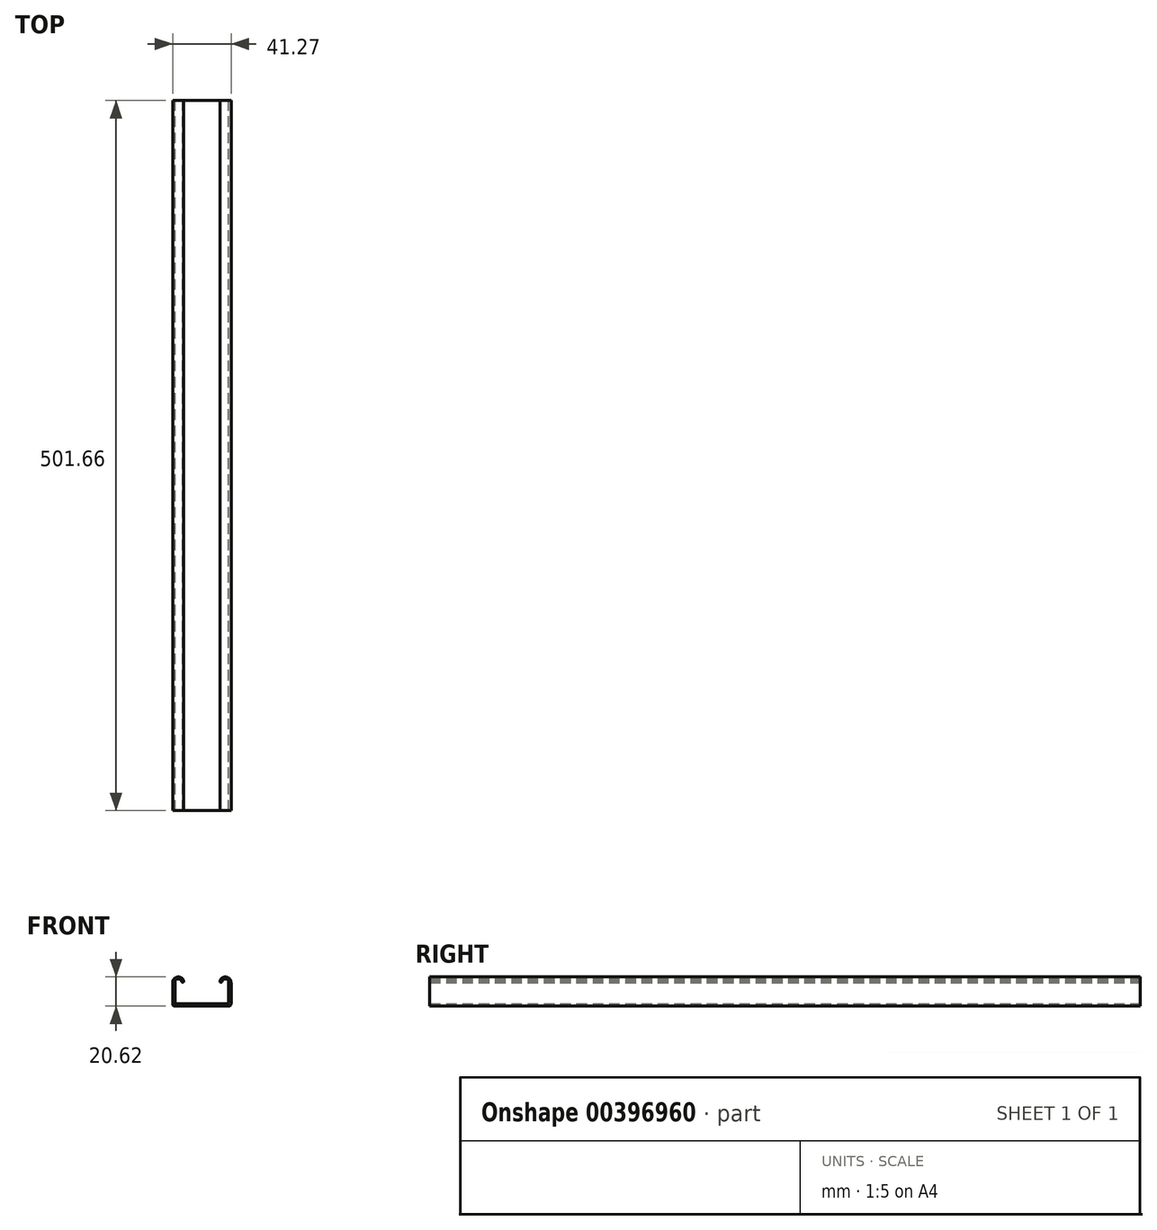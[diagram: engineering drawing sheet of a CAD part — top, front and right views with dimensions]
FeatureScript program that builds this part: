
annotation { "Feature Type Name" : "Feature", "Feature Type Description" : "" }
export const myFeature = defineFeature(function(context is Context, id is Id, definition is map)
    precondition{}
    {
        {
            var Q0;
            Q0=qCreatedBy(makeId("Front.planeOp"),FACE);
            var sketch = newSketch(context, id + "F0", { "sketchPlane" : qUnion([Q0])});
            skLineSegment(sketch, "E0.bottom", {"start": v(0, 6.36) * mm, "end": v(41.28, 6.36) * mm});
            skLineSegment(sketch, "E0.left", {"start": v(0, 6.36) * mm, "end": v(0, 23.02) * mm});
            skLineSegment(sketch, "E0.right", {"start": v(41.28, 6.36) * mm, "end": v(41.28, 23.02) * mm});
            skLineSegment(sketch, "E1.0", {"start": v(1.59, 7.95) * mm, "end": v(1.59, 24.1) * mm});
            skLineSegment(sketch, "E2.0", {"start": v(1.59, 7.95) * mm, "end": v(39.69, 7.95) * mm});
            skLineSegment(sketch, "E3.0", {"start": v(39.69, 7.95) * mm, "end": v(39.69, 24.1) * mm});
            skArc(sketch, "E4", {"start": v(7.92, 23.1) * mm, "mid": v(3.92, 26.98) * mm, "end": v(0, 23.02) * mm});
            skArc(sketch, "E5", {"start": v(6.57, 23.1) * mm, "mid": v(4.48, 25.58) * mm, "end": v(1.59, 24.1) * mm});
            skArc(sketch, "E6.MirrorC", {"start": v(33.35, 23.1) * mm, "mid": v(37.35, 26.98) * mm, "end": v(41.28, 23.02) * mm});
            skArc(sketch, "E7.MirrorC", {"start": v(34.7, 23.1) * mm, "mid": v(36.8, 25.58) * mm, "end": v(39.69, 24.1) * mm});
            skLineSegment(sketch, "E8", {"start": v(6.57, 23.1) * mm, "end": v(7.92, 23.1) * mm});
            skLineSegment(sketch, "E9.trimOffspring", {"start": v(33.35, 23.1) * mm, "end": v(34.7, 23.1) * mm});
            skPoint(sketch, "E10.orphan", {"position": v(20.64, 26.98) * mm});
            skPoint(sketch, "E11.orphan", {"position": v(41.28, 26.98) * mm});
            skLineSegment(sketch, "E12.trimOffspring", {"start": v(39.69, 23.1) * mm, "end": v(39.92, 23.1) * mm});
            skLineSegment(sketch, "E13.trimOffspring", {"start": v(41.28, 7.95) * mm, "end": v(41.53, 7.95) * mm});
            skPoint(sketch, "E14.end.orphan", {"position": v(20.64, 6.36) * mm});
            skPoint(sketch, "E15.orphan", {"position": v(0, 26.98) * mm});
            skSolve(sketch);
        }
        {
            var Q0;
            Q0 = qSketchRegion(id + "F0", true);
            extrude(context, id + "F1", {"entities" : qUnion([Q0]), "endBound" : BoundingType.SYMMETRIC, "depth" : 501.65 * mm});
        }
        {
            var Q0;
            Q0=makeQuery(id+"F1.opExtrude","SWEPT_EDGE",EDGE,{"disambiguationData":[OSD([sQuery(id+"F0.wireOp",EDGE,"E2.0"),sQuery(id+"F0.wireOp",EDGE,"E3.0")])]});
            var Q1;
            Q1=makeQuery(id+"F1.opExtrude","SWEPT_EDGE",EDGE,{"disambiguationData":[OSD([sQuery(id+"F0.wireOp",EDGE,"E1.0"),sQuery(id+"F0.wireOp",EDGE,"E2.0")])]});
            var Q2;
            Q2=makeQuery(id+"F1.opExtrude","SWEPT_EDGE",EDGE,{"disambiguationData":[OSD([sQuery(id+"F0.wireOp",EDGE,"E0.bottom"),sQuery(id+"F0.wireOp",EDGE,"E0.left")])]});
            var Q3;
            Q3=makeQuery(id+"F1.opExtrude","SWEPT_EDGE",EDGE,{"disambiguationData":[OSD([sQuery(id+"F0.wireOp",EDGE,"E0.bottom"),sQuery(id+"F0.wireOp",EDGE,"E0.right")])]});
            fillet(context, id + "F2", {"entities" : qUnion([Q0, Q1, Q2, Q3]), "radius" : 1.59 * mm, "tangentPropagation" : true, "allowEdgeOverflow" : false});
        }
        {
            var Q0;
            Q0=makeQuery(id+"F1.opExtrude","SWEPT_EDGE",EDGE,{"disambiguationData":[OSD([sQuery(id+"F0.wireOp",EDGE,"E6.MirrorC"),sQuery(id+"F0.wireOp",EDGE,"E9.trimOffspring")])]});
            var Q1;
            Q1=makeQuery(id+"F1.opExtrude","SWEPT_EDGE",EDGE,{"disambiguationData":[OSD([sQuery(id+"F0.wireOp",EDGE,"E7.MirrorC"),sQuery(id+"F0.wireOp",EDGE,"E9.trimOffspring")])]});
            var Q2;
            Q2=makeQuery(id+"F1.opExtrude","SWEPT_EDGE",EDGE,{"disambiguationData":[OSD([sQuery(id+"F0.wireOp",EDGE,"E4"),sQuery(id+"F0.wireOp",EDGE,"E8")])]});
            var Q3;
            Q3=makeQuery(id+"F1.opExtrude","SWEPT_EDGE",EDGE,{"disambiguationData":[OSD([sQuery(id+"F0.wireOp",EDGE,"E5"),sQuery(id+"F0.wireOp",EDGE,"E8")])]});
            fillet(context, id + "F3", {"entities" : qUnion([Q0, Q1, Q2, Q3]), "radius" : 0.83 * mm, "tangentPropagation" : true, "allowEdgeOverflow" : false});
        }
    });
